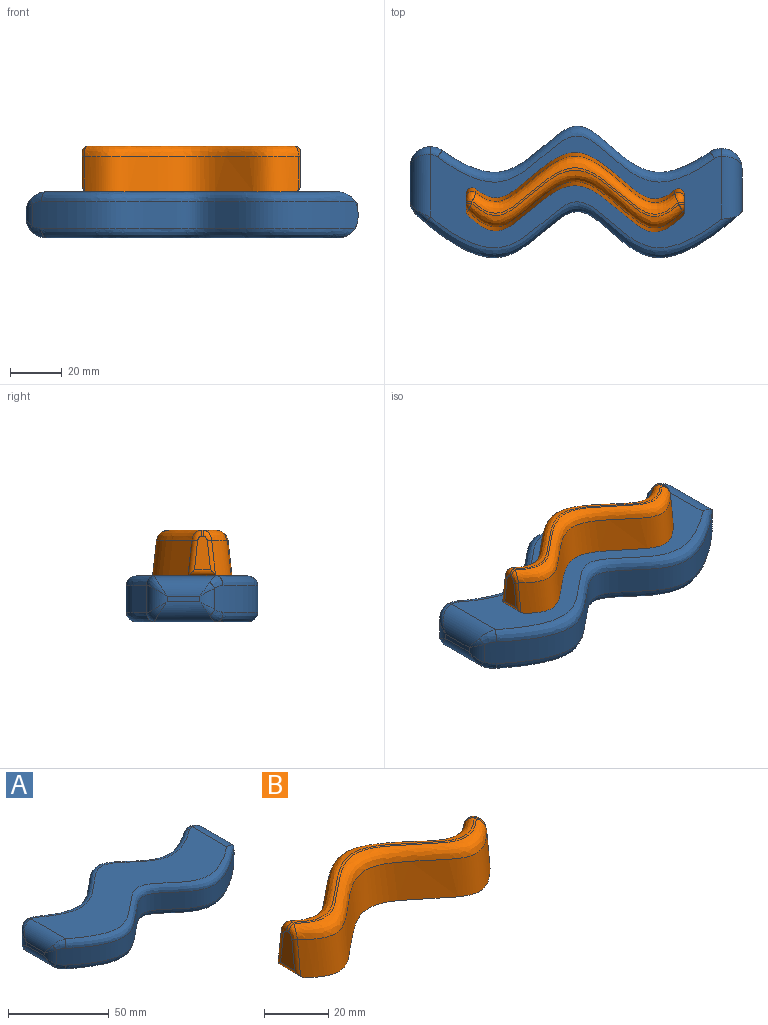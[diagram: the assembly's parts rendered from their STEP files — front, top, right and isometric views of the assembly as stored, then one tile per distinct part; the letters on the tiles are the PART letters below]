
ASSEMBLY  parts=2 mates=1
PART A: 31 faces, bbox 128.3x51x17.8 mm
  f0: plane 16.57x2.03mm, normal (1,0,0), area 33.7mm2, adj f1,f27,f29,f30
  f1: cylinder r=7.87mm len=24.3mm, axis (0,-1,0), area 253.1mm2, adj f0,f2,f24,f25,f26,f30
  f2: bspline ~126.64x21.78mm, area 759.5mm2, adj f1,f3,f24,f30
  f3: bspline ~6x5.19mm, area 25.5mm2, adj f2,f4,f23,f30
  f4: cylinder r=7.87mm len=24.19mm, axis (0,1,0), area 231.6mm2, adj f3,f5,f22,f23,f24
  f5: plane 12.68x2.03mm, normal (-1,0,0), area 25.8mm2, adj f4,f6,f20,f21
  f6: cylinder r=7.87mm len=8.24mm, axis (0,0,1), area 33mm2, adj f5,f7,f23,f30
  f7: bspline ~5.74x5.27mm, area 7.1mm2, adj f6,f8,f20
  f8: bspline ~6x5.19mm, area 25.5mm2, adj f7,f9,f20,f30
  f9: bspline ~126.64x21.78mm, area 767.6mm2, adj f8,f10,f29,f30
  f10: plane 113.48x43.46mm, normal (0,0,-1), area 2855.2mm2, adj f9,f11,f13,f18,f20,f29
  f11: bspline ~4.43x3.95mm, area 21.8mm2, adj f10,f12,f13,f27
  f12: bspline ~7.57x6.41mm, area 23.3mm2, adj f11,f27,f29
  f13: bspline ~123.48x21.78mm, area 675.8mm2, adj f10,f11,f14,f18
  f14: bspline ~118.51x17.97mm, area 1200.4mm2, adj f13,f15,f21,f27
  f15: bspline ~123.48x21.78mm, area 675.8mm2, adj f14,f16,f17,f24
  f16: bspline ~4.43x3.95mm, area 21.8mm2, adj f15,f24,f26,f27
  f17: bspline ~4.57x3.97mm, area 22.5mm2, adj f15,f21,f22,f24
  f18: bspline ~4.57x3.97mm, area 22.5mm2, adj f10,f13,f19,f21
  f19: bspline ~7.87x7.87mm, area 27.4mm2, adj f18,f20,f21
  f20: cylinder r=7.87mm len=24.19mm, axis (0,1,0), area 231.6mm2, adj f5,f7,f8,f10,f19
  f21: cylinder r=7.87mm len=12.44mm, axis (0,0,-1), area 147.3mm2, adj f5,f14,f17,f18,f19,f22
  f22: bspline ~7.87x7.87mm, area 26.9mm2, adj f4,f17,f21
  f23: bspline ~5.74x5.27mm, area 7mm2, adj f3,f4,f6
  f24: plane 113.48x43.46mm, normal (0,0,1), area 2855.2mm2, adj f1,f2,f4,f15,f16,f17
  f25: bspline ~3.73x3.62mm, area 0.6mm2, adj f1,f27
  f26: bspline ~7.35x5.98mm, area 22mm2, adj f1,f16,f27
  f27: cylinder r=7.87mm len=12.3mm, axis (0,0,-1), area 140.9mm2, adj f0,f11,f12,f14,f16,f25,f26,f28
  f28: bspline ~3.03x2.5mm, area 0.3mm2, adj f27,f29
  f29: cylinder r=7.87mm len=24.3mm, axis (0,-1,0), area 257.1mm2, adj f0,f9,f10,f12,f28,f30
  f30: bspline ~125.76x17.78mm, area 1499.6mm2, adj f0,f1,f2,f3,f6,f8,f9,f29
PART B: 20 faces, bbox 84.4x30.9x18.5 mm
  f0: plane 13.11x6.11mm, normal (1,0,0), area 60.5mm2, adj f14,f15,f16,f17,f18,f19
  f1: plane 13.11x6.15mm, normal (-1,0,0), area 61.1mm2, adj f8,f9,f10,f11,f12,f13
  f2: plane 81.74x30.91mm, normal (0,0,-1), area 1012.2mm2, adj f3,f7,f12,f13,f18,f19
  f3: bspline ~84.33x19.66mm, area 1340mm2, adj f2,f4,f10,f12,f16,f18
  f4: bspline ~84.33x22.6mm, area 577.3mm2, adj f3,f5,f8,f14
  f5: plane 81.71x19.09mm, normal (0,0,1), area 72.3mm2, adj f4,f6,f9,f15
  f6: bspline ~84.33x22.6mm, area 545.9mm2, adj f5,f7,f11,f17
  f7: bspline ~84.33x19.66mm, area 1233.3mm2, adj f2,f6,f13,f19
  f8: bspline ~4.31x3.15mm, area 9.8mm2, adj f1,f4,f9,f10
  f9: cylinder r=2.29mm len=2.29mm, axis (0,1,0), area 3.3mm2, adj f1,f5,f8,f11
  f10: cylinder r=2.29mm len=13.3mm, axis (0,0.11,0.99), area 23.4mm2, adj f1,f3,f8,f12
  f11: bspline ~6.24x4.86mm, area 23mm2, adj f1,f6,f9,f13
  f12: cylinder r=2.29mm len=12.02mm, axis (0,1,0), area 34.1mm2, adj f1,f2,f3,f10,f13
  f13: cylinder r=2.29mm len=14.01mm, axis (0,0.11,-0.99), area 67.5mm2, adj f1,f2,f7,f11,f12
  f14: bspline ~4.29x3.1mm, area 9.6mm2, adj f0,f4,f15,f16
  f15: cylinder r=2.29mm len=2.29mm, axis (0,-1,0), area 3.3mm2, adj f0,f5,f14,f17
  f16: cylinder r=2.29mm len=13.29mm, axis (0,0.11,0.99), area 23.2mm2, adj f0,f3,f14,f18
  f17: bspline ~6.25x4.87mm, area 23mm2, adj f0,f6,f15,f19
  f18: cylinder r=2.29mm len=12mm, axis (0,-1,0), area 34mm2, adj f0,f2,f3,f16,f19
  f19: cylinder r=2.29mm len=14.01mm, axis (0,0.11,-0.99), area 67.7mm2, adj f0,f2,f7,f17,f18
PLACE A t=(13.16,12.4,56.71)mm
PLACE B t=(-9.09,13.58,14.26)mm
MATE fastened A.f24 <-> B.f2  axis (0,0,1) through (-51.19,-16.85,15.89)mm
